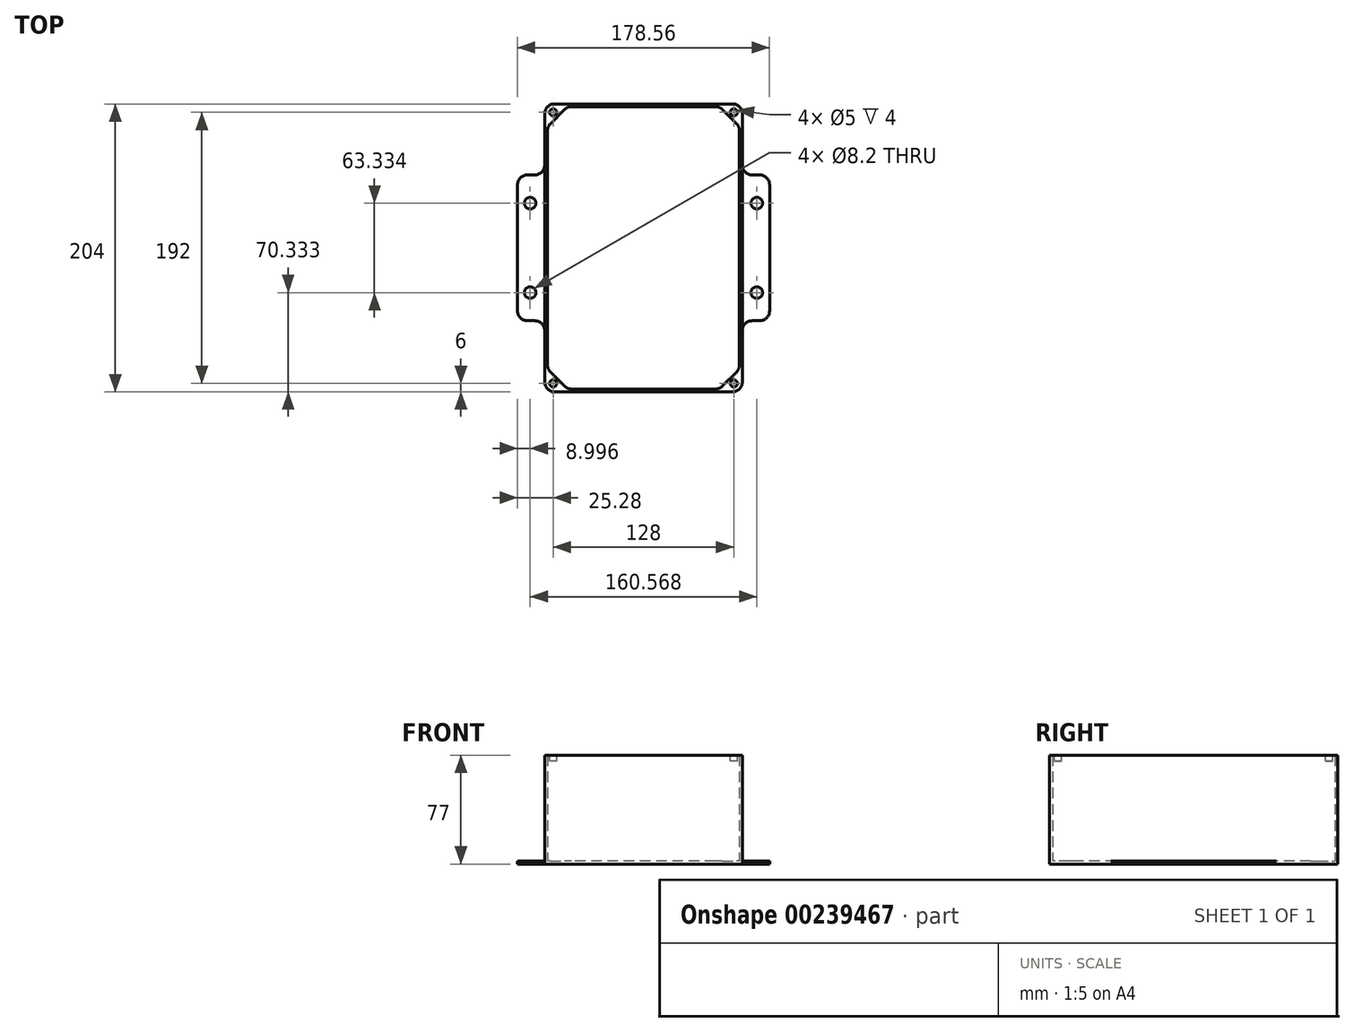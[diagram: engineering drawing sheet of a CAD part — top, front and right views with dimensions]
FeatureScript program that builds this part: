
annotation { "Feature Type Name" : "Feature", "Feature Type Description" : "" }
export const myFeature = defineFeature(function(context is Context, id is Id, definition is map)
    precondition{}
    {
        {
            var Q0;
            Q0=qCreatedBy(makeId("Top.planeOp"),FACE);
            var sketch = newSketch(context, id + "F0", { "sketchPlane" : qUnion([Q0])});
            skLineSegment(sketch, "E0.bottom", {"start": v(70, 102) * mm, "end": v(-70, 102) * mm});
            skLineSegment(sketch, "E0.top", {"start": v(70, -102) * mm, "end": v(-70, -102) * mm});
            skLineSegment(sketch, "E0.left", {"start": v(70, 102) * mm, "end": v(70, -102) * mm});
            skLineSegment(sketch, "E0.right", {"start": v(-70, 102) * mm, "end": v(-70, -102) * mm});
            skPoint(sketch, "E0.middle", {"position": v(0, 0) * mm});
            skLineSegment(sketch, "E1.bottom", {"start": v(89.28, 51.67) * mm, "end": v(-89.28, 51.67) * mm});
            skLineSegment(sketch, "E1.top", {"start": v(89.28, -51.67) * mm, "end": v(-89.28, -51.67) * mm});
            skLineSegment(sketch, "E1.left", {"start": v(89.28, 51.67) * mm, "end": v(89.28, -51.67) * mm});
            skLineSegment(sketch, "E1.right", {"start": v(-89.28, 51.67) * mm, "end": v(-89.28, -51.67) * mm});
            skSolve(sketch);
        }
        {
            var Q0;
            {var subQ0=sQuery(id+"F0.wireOp",EDGE,"E0.bottom");Q0=makeQuery(id+"F0.imprint","IMPRINT",FACE,{"disambiguationData":[TD([[makeQuery(id+"F0.imprint","IMPRINT",EDGE,{"derivedFrom":subQ0}),1.0]])]});}
            var Q1;
            {var subQ0=sQuery(id+"F0.wireOp",EDGE,"E1.bottom");var subQ1=sQuery(id+"F0.wireOp",EDGE,"E0.left");var subQ2=makeQuery(id+"F0.imprint","INTERSECT",VERTEX,{"derivedFrom":[subQ1,subQ0]});Q1=makeQuery(id+"F0.imprint","IMPRINT",FACE,{"disambiguationData":[TD([[makeQuery(id+"F0.imprint","IMPRINT",EDGE,{"disambiguationData":[TD([[subQ2,-1.0]])],"derivedFrom":subQ1}),-1.0]])]});}
            var Q2;
            {var subQ5=sQuery(id+"F0.wireOp",EDGE,"E1.right");Q2=makeQuery(id+"F0.imprint","IMPRINT",FACE,{"disambiguationData":[TD([[makeQuery(id+"F0.imprint","IMPRINT",EDGE,{"derivedFrom":subQ5}),1.0]])]});}
            var Q3;
            {var subQ0=sQuery(id+"F0.wireOp",EDGE,"E0.top");Q3=makeQuery(id+"F0.imprint","IMPRINT",FACE,{"disambiguationData":[TD([[makeQuery(id+"F0.imprint","IMPRINT",EDGE,{"derivedFrom":subQ0}),-1.0]])]});}
            var Q4;
            {var subQ5=sQuery(id+"F0.wireOp",EDGE,"E1.left");Q4=makeQuery(id+"F0.imprint","IMPRINT",FACE,{"disambiguationData":[TD([[makeQuery(id+"F0.imprint","IMPRINT",EDGE,{"derivedFrom":subQ5}),-1.0]])]});}
            extrude(context, id + "F1", {"entities" : qUnion([Q0, Q1, Q2, Q3, Q4]), "depth" : 2 * mm});
        }
        {
            var Q0;
            Q0=makeQuery(id+"F1.opExtrude","CAP_FACE",FACE,{"disambiguationData":[OSD([sQuery(id+"F0.wireOp",EDGE,"E0.bottom"),sQuery(id+"F0.wireOp",EDGE,"E0.top"),sQuery(id+"F0.wireOp",EDGE,"E0.left"),sQuery(id+"F0.wireOp",EDGE,"E0.right"),sQuery(id+"F0.wireOp",EDGE,"E1.bottom"),sQuery(id+"F0.wireOp",EDGE,"E1.top"),sQuery(id+"F0.wireOp",EDGE,"E1.left"),sQuery(id+"F0.wireOp",EDGE,"E1.right")])],"isStart":false});
            var sketch = newSketch(context, id + "F2", { "sketchPlane" : qUnion([Q0])});
            skLineSegment(sketch, "E2.bottom", {"start": v(70, 102) * mm, "end": v(-70, 102) * mm});
            skLineSegment(sketch, "E2.top", {"start": v(70, -102) * mm, "end": v(-70, -102) * mm});
            skLineSegment(sketch, "E2.left", {"start": v(70, 102) * mm, "end": v(70, -102) * mm});
            skLineSegment(sketch, "E2.right", {"start": v(-70, 102) * mm, "end": v(-70, -102) * mm});
            skPoint(sketch, "E2.middle", {"position": v(0, 0) * mm});
            skLineSegment(sketch, "E3.bottom", {"start": v(68, 100) * mm, "end": v(-68, 100) * mm});
            skLineSegment(sketch, "E3.top", {"start": v(68, -100) * mm, "end": v(-68, -100) * mm});
            skLineSegment(sketch, "E3.left", {"start": v(68, 100) * mm, "end": v(68, -100) * mm});
            skLineSegment(sketch, "E3.right", {"start": v(-68, 100) * mm, "end": v(-68, -100) * mm});
            skLineSegment(sketch, "E4", {"start": v(53.86, 100) * mm, "end": v(68, 85.86) * mm});
            skLineSegment(sketch, "E5", {"start": v(-68, 85.86) * mm, "end": v(-53.86, 100) * mm});
            skLineSegment(sketch, "E6", {"start": v(68, -85.86) * mm, "end": v(53.86, -100) * mm});
            skLineSegment(sketch, "E7", {"start": v(-68, -85.86) * mm, "end": v(-53.86, -100) * mm});
            skSolve(sketch);
        }
        {
            var Q0;
            {var subQ3=sQuery(id+"F2.wireOp",EDGE,"E5");Q0=makeQuery(id+"F2.imprint","IMPRINT",FACE,{"disambiguationData":[TD([[makeQuery(id+"F2.imprint","IMPRINT",EDGE,{"derivedFrom":subQ3}),1.0]])]});}
            var Q1;
            {var subQ13=sQuery(id+"F2.wireOp",EDGE,"E2.bottom");Q1=makeQuery(id+"F2.imprint","IMPRINT",FACE,{"disambiguationData":[TD([[makeQuery(id+"F2.imprint","IMPRINT",EDGE,{"derivedFrom":subQ13}),1.0]])]});}
            var Q2;
            {var subQ3=sQuery(id+"F2.wireOp",EDGE,"E4");Q2=makeQuery(id+"F2.imprint","IMPRINT",FACE,{"disambiguationData":[TD([[makeQuery(id+"F2.imprint","IMPRINT",EDGE,{"derivedFrom":subQ3}),1.0]])]});}
            var Q3;
            {var subQ3=sQuery(id+"F2.wireOp",EDGE,"E6");Q3=makeQuery(id+"F2.imprint","IMPRINT",FACE,{"disambiguationData":[TD([[makeQuery(id+"F2.imprint","IMPRINT",EDGE,{"derivedFrom":subQ3}),1.0]])]});}
            var Q4;
            {var subQ3=sQuery(id+"F2.wireOp",EDGE,"E7");Q4=makeQuery(id+"F2.imprint","IMPRINT",FACE,{"disambiguationData":[TD([[makeQuery(id+"F2.imprint","IMPRINT",EDGE,{"derivedFrom":subQ3}),-1.0]])]});}
            extrude(context, id + "F3", {"entities" : qUnion([Q0, Q1, Q2, Q3, Q4]), "operationType" : NewBodyOperationType.ADD, "depth" : 75 * mm});
        }
        {
            var Q0;
            Q0=makeQuery(id+"F3.boolean.opBoolean","MERGE",EDGE,{"derivedFrom":[makeQuery(id+"F1.opExtrude","SWEPT_EDGE",EDGE,{"disambiguationData":[OSD([sQuery(id+"F0.wireOp",EDGE,"E0.top"),sQuery(id+"F0.wireOp",EDGE,"E0.left")])]}),makeQuery(id+"F3.opExtrude","SWEPT_EDGE",EDGE,{"disambiguationData":[OSD([sQuery(id+"F2.wireOp",EDGE,"E2.top"),sQuery(id+"F2.wireOp",EDGE,"E2.left")])]})]});
            var Q1;
            Q1=makeQuery(id+"F3.boolean.opBoolean","MERGE",EDGE,{"derivedFrom":[makeQuery(id+"F1.opExtrude","SWEPT_EDGE",EDGE,{"disambiguationData":[OSD([sQuery(id+"F0.wireOp",EDGE,"E0.bottom"),sQuery(id+"F0.wireOp",EDGE,"E0.left")])]}),makeQuery(id+"F3.opExtrude","SWEPT_EDGE",EDGE,{"disambiguationData":[OSD([sQuery(id+"F2.wireOp",EDGE,"E2.bottom"),sQuery(id+"F2.wireOp",EDGE,"E2.left")])]})]});
            var Q2;
            Q2=makeQuery(id+"F3.boolean.opBoolean","MERGE",EDGE,{"derivedFrom":[makeQuery(id+"F1.opExtrude","SWEPT_EDGE",EDGE,{"disambiguationData":[OSD([sQuery(id+"F0.wireOp",EDGE,"E0.bottom"),sQuery(id+"F0.wireOp",EDGE,"E0.right")])]}),makeQuery(id+"F3.opExtrude","SWEPT_EDGE",EDGE,{"disambiguationData":[OSD([sQuery(id+"F2.wireOp",EDGE,"E2.bottom"),sQuery(id+"F2.wireOp",EDGE,"E2.right")])]})]});
            var Q3;
            Q3=makeQuery(id+"F3.boolean.opBoolean","MERGE",EDGE,{"derivedFrom":[makeQuery(id+"F1.opExtrude","SWEPT_EDGE",EDGE,{"disambiguationData":[OSD([sQuery(id+"F0.wireOp",EDGE,"E0.top"),sQuery(id+"F0.wireOp",EDGE,"E0.right")])]}),makeQuery(id+"F3.opExtrude","SWEPT_EDGE",EDGE,{"disambiguationData":[OSD([sQuery(id+"F2.wireOp",EDGE,"E2.top"),sQuery(id+"F2.wireOp",EDGE,"E2.right")])]})]});
            var Q4;
            Q4=makeQuery(id+"F3.opExtrude","SWEPT_EDGE",EDGE,{"disambiguationData":[OSD([sQuery(id+"F2.wireOp",EDGE,"E3.top"),sQuery(id+"F2.wireOp",EDGE,"E7")])]});
            var Q5;
            Q5=makeQuery(id+"F3.opExtrude","SWEPT_EDGE",EDGE,{"disambiguationData":[OSD([sQuery(id+"F2.wireOp",EDGE,"E3.right"),sQuery(id+"F2.wireOp",EDGE,"E7")])]});
            var Q6;
            Q6=makeQuery(id+"F3.opExtrude","SWEPT_EDGE",EDGE,{"disambiguationData":[OSD([sQuery(id+"F2.wireOp",EDGE,"E3.top"),sQuery(id+"F2.wireOp",EDGE,"E6")])]});
            var Q7;
            Q7=makeQuery(id+"F3.opExtrude","SWEPT_EDGE",EDGE,{"disambiguationData":[OSD([sQuery(id+"F2.wireOp",EDGE,"E3.left"),sQuery(id+"F2.wireOp",EDGE,"E6")])]});
            var Q8;
            Q8=makeQuery(id+"F3.opExtrude","SWEPT_EDGE",EDGE,{"disambiguationData":[OSD([sQuery(id+"F2.wireOp",EDGE,"E3.right"),sQuery(id+"F2.wireOp",EDGE,"E5")])]});
            var Q9;
            Q9=makeQuery(id+"F3.opExtrude","SWEPT_EDGE",EDGE,{"disambiguationData":[OSD([sQuery(id+"F2.wireOp",EDGE,"E3.bottom"),sQuery(id+"F2.wireOp",EDGE,"E5")])]});
            var Q10;
            Q10=makeQuery(id+"F3.opExtrude","SWEPT_EDGE",EDGE,{"disambiguationData":[OSD([sQuery(id+"F2.wireOp",EDGE,"E3.bottom"),sQuery(id+"F2.wireOp",EDGE,"E4")])]});
            var Q11;
            Q11=makeQuery(id+"F3.opExtrude","SWEPT_EDGE",EDGE,{"disambiguationData":[OSD([sQuery(id+"F2.wireOp",EDGE,"E3.left"),sQuery(id+"F2.wireOp",EDGE,"E4")])]});
            var Q12;
            Q12=makeQuery(id+"F1.opExtrude","SWEPT_EDGE",EDGE,{"disambiguationData":[OSD([sQuery(id+"F0.wireOp",EDGE,"E0.right"),sQuery(id+"F0.wireOp",EDGE,"E1.bottom")])]});
            var Q13;
            Q13=makeQuery(id+"F1.opExtrude","SWEPT_EDGE",EDGE,{"disambiguationData":[OSD([sQuery(id+"F0.wireOp",EDGE,"E1.bottom"),sQuery(id+"F0.wireOp",EDGE,"E1.right")])]});
            var Q14;
            Q14=makeQuery(id+"F1.opExtrude","SWEPT_EDGE",EDGE,{"disambiguationData":[OSD([sQuery(id+"F0.wireOp",EDGE,"E1.top"),sQuery(id+"F0.wireOp",EDGE,"E1.right")])]});
            var Q15;
            Q15=makeQuery(id+"F1.opExtrude","SWEPT_EDGE",EDGE,{"disambiguationData":[OSD([sQuery(id+"F0.wireOp",EDGE,"E0.right"),sQuery(id+"F0.wireOp",EDGE,"E1.top")])]});
            var Q16;
            Q16=makeQuery(id+"F1.opExtrude","SWEPT_EDGE",EDGE,{"disambiguationData":[OSD([sQuery(id+"F0.wireOp",EDGE,"E0.left"),sQuery(id+"F0.wireOp",EDGE,"E1.top")])]});
            var Q17;
            Q17=makeQuery(id+"F1.opExtrude","SWEPT_EDGE",EDGE,{"disambiguationData":[OSD([sQuery(id+"F0.wireOp",EDGE,"E1.top"),sQuery(id+"F0.wireOp",EDGE,"E1.left")])]});
            var Q18;
            Q18=makeQuery(id+"F1.opExtrude","SWEPT_EDGE",EDGE,{"disambiguationData":[OSD([sQuery(id+"F0.wireOp",EDGE,"E1.bottom"),sQuery(id+"F0.wireOp",EDGE,"E1.left")])]});
            var Q19;
            Q19=makeQuery(id+"F1.opExtrude","SWEPT_EDGE",EDGE,{"disambiguationData":[OSD([sQuery(id+"F0.wireOp",EDGE,"E0.left"),sQuery(id+"F0.wireOp",EDGE,"E1.bottom")])]});
            fillet(context, id + "F4", {"entities" : qUnion([Q0, Q1, Q2, Q3, Q4, Q5, Q6, Q7, Q8, Q9, Q10, Q11, Q12, Q13, Q14, Q15, Q16, Q17, Q18, Q19]), "radius" : 7 * mm, "tangentPropagation" : true, "allowEdgeOverflow" : false});
        }
        {
            var Q0;
            Q0=makeQuery(id+"F3.opExtrude","CAP_FACE",FACE,{"disambiguationData":[OSD([sQuery(id+"F2.wireOp",EDGE,"E2.bottom"),sQuery(id+"F2.wireOp",EDGE,"E2.top"),sQuery(id+"F2.wireOp",EDGE,"E2.left"),sQuery(id+"F2.wireOp",EDGE,"E2.right"),sQuery(id+"F2.wireOp",EDGE,"E3.bottom"),sQuery(id+"F2.wireOp",EDGE,"E3.top"),sQuery(id+"F2.wireOp",EDGE,"E3.left"),sQuery(id+"F2.wireOp",EDGE,"E3.right"),sQuery(id+"F2.wireOp",EDGE,"E4"),sQuery(id+"F2.wireOp",EDGE,"E5"),sQuery(id+"F2.wireOp",EDGE,"E6"),sQuery(id+"F2.wireOp",EDGE,"E7")])],"isStart":false});
            var sketch = newSketch(context, id + "F5", { "sketchPlane" : qUnion([Q0])});
            skCircle(sketch, "E8", {"center": v(-64, 96) * mm, "radius": 2.5 * mm});
            skCircle(sketch, "E9", {"center": v(64, 96) * mm, "radius": 2.5 * mm});
            skCircle(sketch, "E10", {"center": v(-64, -96) * mm, "radius": 2.5 * mm});
            skCircle(sketch, "E11", {"center": v(64, -96) * mm, "radius": 2.5 * mm});
            skSolve(sketch);
        }
        {
            var Q0;
            Q0=makeQuery(id+"F5.imprint","IMPRINT",FACE,{"disambiguationData":[TD([[makeQuery(id+"F5.imprint","IMPRINT",EDGE,{"derivedFrom":sQuery(id+"F5.wireOp",EDGE,"E8")}),1.0]])]});
            var Q1;
            Q1=makeQuery(id+"F5.imprint","IMPRINT",FACE,{"disambiguationData":[TD([[makeQuery(id+"F5.imprint","IMPRINT",EDGE,{"derivedFrom":sQuery(id+"F5.wireOp",EDGE,"E9")}),1.0]])]});
            var Q2;
            Q2=makeQuery(id+"F5.imprint","IMPRINT",FACE,{"disambiguationData":[TD([[makeQuery(id+"F5.imprint","IMPRINT",EDGE,{"derivedFrom":sQuery(id+"F5.wireOp",EDGE,"E11")}),1.0]])]});
            var Q3;
            Q3=makeQuery(id+"F5.imprint","IMPRINT",FACE,{"disambiguationData":[TD([[makeQuery(id+"F5.imprint","IMPRINT",EDGE,{"derivedFrom":sQuery(id+"F5.wireOp",EDGE,"E10")}),1.0]])]});
            var Q4;
            Q4=sQuery(id+"F5.wireOp",EDGE,"E8");
            var Q5;
            Q5=sQuery(id+"F5.wireOp",EDGE,"E9");
            var Q6;
            Q6=sQuery(id+"F5.wireOp",EDGE,"E11");
            var Q7;
            Q7=sQuery(id+"F5.wireOp",EDGE,"E10");
            extrude(context, id + "F6", {"entities" : qUnion([Q0, Q1, Q2, Q3]), "operationType" : NewBodyOperationType.REMOVE, "surfaceEntities" : qUnion([Q4, Q5, Q6, Q7]), "oppositeDirection" : true, "depth" : 4 * mm});
        }
        {
            var Q0;
            {var subQ0=sQuery(id+"F0.wireOp",EDGE,"E1.right");var subQ1=sQuery(id+"F0.wireOp",EDGE,"E1.top");var subQ2=sQuery(id+"F0.wireOp",EDGE,"E0.right");var subQ4=sQuery(id+"F0.wireOp",EDGE,"E1.bottom");var subQ6=sQuery(id+"F0.wireOp",EDGE,"E0.top");var subQ7=sQuery(id+"F0.wireOp",EDGE,"E0.bottom");Q0=makeQuery(id+"F3.boolean.opBoolean","SPLIT",FACE,{"disambiguationData":[TD([makeQuery(id+"F1.opExtrude","SWEPT_FACE",FACE,{"disambiguationData":[OSD([subQ0])]})])],"derivedFrom":makeQuery(id+"F1.opExtrude","CAP_FACE",FACE,{"disambiguationData":[OSD([subQ7,subQ6,sQuery(id+"F0.wireOp",EDGE,"E0.left"),subQ2,subQ4,subQ1,sQuery(id+"F0.wireOp",EDGE,"E1.left"),subQ0])],"isStart":false})});}
            var sketch = newSketch(context, id + "F7", { "sketchPlane" : qUnion([Q0])});
            skCircle(sketch, "E12", {"center": v(-80.28, 31.67) * mm, "radius": 4.1 * mm});
            skCircle(sketch, "E13", {"center": v(-80.28, -31.67) * mm, "radius": 4.1 * mm});
            skCircle(sketch, "E14", {"center": v(80.28, 31.67) * mm, "radius": 4.1 * mm});
            skCircle(sketch, "E15", {"center": v(80.28, -31.67) * mm, "radius": 4.1 * mm});
            skSolve(sketch);
        }
        {
            var Q0;
            Q0=makeQuery(id+"F7.imprint","IMPRINT",FACE,{"disambiguationData":[TD([[makeQuery(id+"F7.imprint","IMPRINT",EDGE,{"derivedFrom":sQuery(id+"F7.wireOp",EDGE,"E12")}),1.0]])]});
            var Q1;
            Q1=makeQuery(id+"F7.imprint","IMPRINT",FACE,{"disambiguationData":[TD([[makeQuery(id+"F7.imprint","IMPRINT",EDGE,{"derivedFrom":sQuery(id+"F7.wireOp",EDGE,"E13")}),1.0]])]});
            var Q2;
            Q2=makeQuery(id+"F7.imprint","IMPRINT",FACE,{"disambiguationData":[TD([[makeQuery(id+"F7.imprint","IMPRINT",EDGE,{"derivedFrom":sQuery(id+"F7.wireOp",EDGE,"E15")}),1.0]])]});
            var Q3;
            Q3=makeQuery(id+"F7.imprint","IMPRINT",FACE,{"disambiguationData":[TD([[makeQuery(id+"F7.imprint","IMPRINT",EDGE,{"derivedFrom":sQuery(id+"F7.wireOp",EDGE,"E14")}),1.0]])]});
            extrude(context, id + "F8", {"entities" : qUnion([Q0, Q1, Q2, Q3]), "operationType" : NewBodyOperationType.REMOVE, "oppositeDirection" : true, "depth" : 25 * mm});
        }
    });
